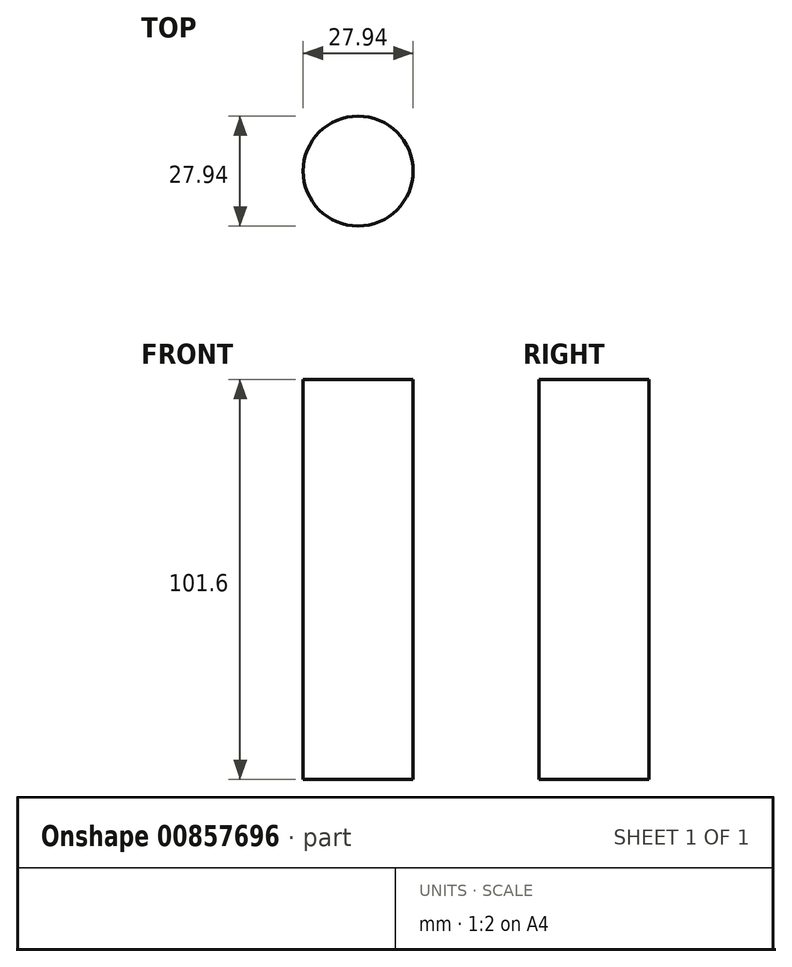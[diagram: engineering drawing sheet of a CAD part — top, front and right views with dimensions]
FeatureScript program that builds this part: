
annotation { "Feature Type Name" : "Feature", "Feature Type Description" : "" }
export const myFeature = defineFeature(function(context is Context, id is Id, definition is map)
    precondition{}
    {
        {
            var Q0;
            Q0=qCreatedBy(makeId("Front.planeOp"),FACE);
            var sketch = newSketch(context, id + "F0", { "sketchPlane" : qUnion([Q0])});
            skLineSegment(sketch, "E0", {"start": v(0, 0) * mm, "end": v(0, 101.6) * mm});
            skLineSegment(sketch, "E1", {"start": v(0, 0) * mm, "end": v(13.97, 0) * mm});
            skLineSegment(sketch, "E2", {"start": v(13.97, 0) * mm, "end": v(13.97, 101.6) * mm});
            skLineSegment(sketch, "E3", {"start": v(0, 101.6) * mm, "end": v(13.97, 101.6) * mm});
            skLineSegment(sketch, "E4", {"start": v(0, 0) * mm, "end": v(0, 119.26) * mm});
            skSolve(sketch);
        }
        {
            var Q0;
            {var subQ0=sQuery(id+"F0.wireOp",EDGE,"E1");Q0=makeQuery(id+"F0.imprint","IMPRINT",FACE,{"disambiguationData":[TD([[makeQuery(id+"F0.imprint","IMPRINT",EDGE,{"derivedFrom":subQ0}),1.0]])]});}
            var Q1;
            Q1=sQuery(id+"F0.wireOp",EDGE,"E4");
            revolve(context, id + "F1", {"surfaceOperationType" : NewSurfaceOperationType.NEW, "entities" : qUnion([Q0]), "axis" : qUnion([Q1]), "revolveType" : RevolveType.FULL});
        }
    });
